# Revit family: Shower-Handshower_Kit-KOHLER-FINIAL-K-72654T_1
name_source: partatom
category: Plumbing Fixtures
revit_build: Autodesk Revit 2017 (Build: 20160225_1515(x64)
units: mm (PartAtom-declared; Revit-internal decimal feet)

## family parameters
Cut with Voids When Loaded = No
Host = Face
OmniClass Number = 23.31.17.00
OmniClass Title = Showers
Part Type = Normal
Room Calculation Point = No
Round Connector Dimension = Use Diameter
Shared = No

## types (6) — shared parameters
ADA Compliant = No
Assembly Code = D2010700
CW Connection = Yes
Cold Water Inlet = Cold Water Inlet
Date Modified = 25/09/2020
Default Elevation = 42"
Drain Included = No
Flow Rate = 0 GPM
HW Connection = Yes
Handle Clearance = 3 13/16"
Height = 28"
Hot Water Inlet = Hot Water Inlet
Length = 10 15/16"
Manufacturer = KOHLER Co.
Master Format 2014 = 22 42 23
Master Format 2014 Name = Residential Showers
Material = Premium Metal Construction
Pressure = 0.00 psi
Product Documentation Link = https://files.kohler.com.cn
Product Name = FINIAL
Product Page URL = https://www.kohler.com.cn
Spout Reach = 7 1/2"
URL = http://www.kohler.com.cn
Vent Connection = No
Waste Connection = No
Waste Water Outlet = Waste Water Outlet
WaterSense Certified = No
Width = 5 15/16"

## per-type parameters (varying)
| type | 4P | Description | Finish | Handle Finish | Model | Type |
| Metal Handle, CP-Polished Chrome | No | Wall-hung bathtub shower faucet classic handle | Kohler-Metal-CP-Polished_Chrome | Kohler-Metal-CP-Polished_Chrome | K-72654T-4M-CP | 1 |
| Metal Handle, AF-Flange Gold | No | Wall-hung bathtub shower faucet classic handle | Kohler-Metal-AF-Flange_Gold | Kohler-Metal-AF-Flange_Gold | K-72654T-4M-AF | 2 |
| Metal Handle, SN-Champagne Gold | No | Wall-hung bathtub shower faucet classic handle | Kohler-Metal-SN-Champagne_Gold | Kohler-Metal-SN-Champagne_Gold | K-72654T-4M-SN | 3 |
| Ceramic Handle, CP-Polished Chrome | Yes | Wall-mounted bathtub shower faucet with white classic handle | Kohler-Metal-CP-Polished_Chrome | Kohler-Metal-CP-Polished_Chrome | K-72654T-4P-CP | 6 |
| Metal Handle, R2B-Black Yaojin | No | Wall-hung bathtub shower faucet classic handle | Kohler-Metal-BL-Matte_Black | Kohler-Metal-RGD-Rose_Gold | K-72654T-4M-R2B | 5 |
| Metal Handle,BN-Roman Silver | No | Wall-hung bathtub shower faucet classic handle | Kohler-Metal-BN-Roman_Silver | Kohler-Metal-BN-Roman_Silver | K-72654T-4M-BN | 4 |

## geometry (parser evidence)
native form markers: Sweep x4
no freeform markers — native parametric forms only
